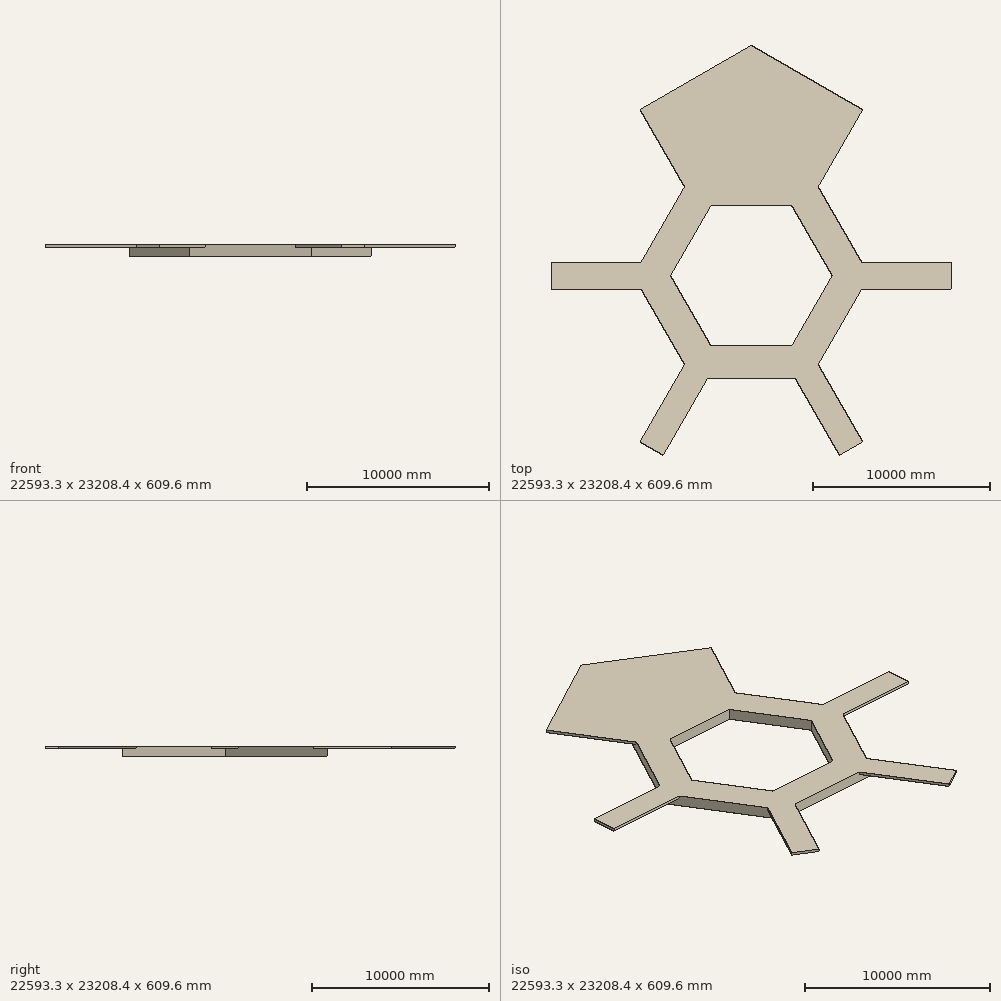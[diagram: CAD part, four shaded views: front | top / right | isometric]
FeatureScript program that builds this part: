
annotation { "Feature Type Name" : "Feature", "Feature Type Description" : "" }
export const myFeature = defineFeature(function(context is Context, id is Id, definition is map)
    precondition{}
    {
        {
            var Q0;
            Q0=qCreatedBy(makeId("Top.planeOp"),FACE);
            var sketch = newSketch(context, id + "F0", { "sketchPlane" : qUnion([Q0])});
            skCircle(sketch, "E0.cCircle", {"center": v(0, 0) * mm, "radius": 4575.39 * mm, "construction": true});
            skLineSegment(sketch, "E0.0", {"start": v(4575.39, 0) * mm, "end": v(2287.7, -3962.4) * mm});
            skLineSegment(sketch, "E0.1", {"start": v(2287.7, -3962.4) * mm, "end": v(-2287.7, -3962.4) * mm});
            skLineSegment(sketch, "E0.2", {"start": v(-2287.7, -3962.4) * mm, "end": v(-4575.39, 0) * mm});
            skLineSegment(sketch, "E0.3", {"start": v(-4575.39, 0) * mm, "end": v(-2287.7, 3962.4) * mm});
            skLineSegment(sketch, "E0.4", {"start": v(-2287.7, 3962.4) * mm, "end": v(2287.7, 3962.4) * mm});
            skLineSegment(sketch, "E0.5", {"start": v(2287.7, 3962.4) * mm, "end": v(4575.39, 0) * mm});
            skCircle(sketch, "E1.cCircle", {"center": v(0, 0) * mm, "radius": 6687.1 * mm, "construction": true});
            skLineSegment(sketch, "E1.0", {"start": v(6687.1, 0) * mm, "end": v(3343.55, -5791.2) * mm});
            skLineSegment(sketch, "E1.1", {"start": v(3343.55, -5791.2) * mm, "end": v(-3343.55, -5791.2) * mm});
            skLineSegment(sketch, "E1.2", {"start": v(-3343.55, -5791.2) * mm, "end": v(-6687.1, 0) * mm});
            skLineSegment(sketch, "E1.3", {"start": v(-6687.1, 0) * mm, "end": v(-3343.55, 5791.2) * mm});
            skLineSegment(sketch, "E1.4", {"start": v(-3343.55, 5791.2) * mm, "end": v(3343.55, 5791.2) * mm});
            skLineSegment(sketch, "E1.5", {"start": v(3343.55, 5791.2) * mm, "end": v(6687.1, 0) * mm});
            skLineSegment(sketch, "E2", {"start": v(-3783.5, 5029.2) * mm, "end": v(-6308.23, 9402.18) * mm});
            skLineSegment(sketch, "E3", {"start": v(-6308.23, 9402.18) * mm, "end": v(-4988.41, 10164.18) * mm});
            skLineSegment(sketch, "E4", {"start": v(-4988.41, 10164.18) * mm, "end": v(-2463.67, 5791.2) * mm});
            skLineSegment(sketch, "E5", {"start": v(-3343.55, 5791.2) * mm, "end": v(-5648.32, 9783.18) * mm, "construction": true});
            skLineSegment(sketch, "E6.1.0", {"start": v(-6687.1, 0) * mm, "end": v(-11296.64, 0) * mm, "construction": true});
            skLineSegment(sketch, "E6.1.1", {"start": v(-11296.64, -762) * mm, "end": v(-11296.64, 762) * mm});
            skLineSegment(sketch, "E6.1.2", {"start": v(-11296.64, 762) * mm, "end": v(-6247.16, 762) * mm});
            skLineSegment(sketch, "E6.1.3", {"start": v(-6247.16, -762) * mm, "end": v(-11296.64, -762) * mm});
            skLineSegment(sketch, "E6.2.0", {"start": v(-3343.55, -5791.2) * mm, "end": v(-5648.32, -9783.18) * mm, "construction": true});
            skLineSegment(sketch, "E6.2.1", {"start": v(-4988.41, -10164.18) * mm, "end": v(-6308.23, -9402.18) * mm});
            skLineSegment(sketch, "E6.2.2", {"start": v(-6308.23, -9402.18) * mm, "end": v(-3783.5, -5029.2) * mm});
            skLineSegment(sketch, "E6.2.3", {"start": v(-2463.67, -5791.2) * mm, "end": v(-4988.41, -10164.18) * mm});
            skLineSegment(sketch, "E6.3.0", {"start": v(3343.55, -5791.2) * mm, "end": v(5648.32, -9783.18) * mm, "construction": true});
            skLineSegment(sketch, "E6.3.1", {"start": v(6308.23, -9402.18) * mm, "end": v(4988.41, -10164.18) * mm});
            skLineSegment(sketch, "E6.3.2", {"start": v(4988.41, -10164.18) * mm, "end": v(2463.67, -5791.2) * mm});
            skLineSegment(sketch, "E6.3.3", {"start": v(3783.5, -5029.2) * mm, "end": v(6308.23, -9402.18) * mm});
            skLineSegment(sketch, "E6.4.0", {"start": v(6687.1, 0) * mm, "end": v(11296.64, 0) * mm, "construction": true});
            skLineSegment(sketch, "E6.4.1", {"start": v(11296.64, 762) * mm, "end": v(11296.64, -762) * mm});
            skLineSegment(sketch, "E6.4.2", {"start": v(11296.64, -762) * mm, "end": v(6247.16, -762) * mm});
            skLineSegment(sketch, "E6.4.3", {"start": v(6247.16, 762) * mm, "end": v(11296.64, 762) * mm});
            skLineSegment(sketch, "E6.5.0", {"start": v(3343.55, 5791.2) * mm, "end": v(5648.32, 9783.18) * mm, "construction": true});
            skLineSegment(sketch, "E6.5.1", {"start": v(4988.41, 10164.18) * mm, "end": v(6308.23, 9402.18) * mm});
            skLineSegment(sketch, "E6.5.2", {"start": v(6308.23, 9402.18) * mm, "end": v(3783.5, 5029.2) * mm});
            skLineSegment(sketch, "E6.5.3", {"start": v(2463.67, 5791.2) * mm, "end": v(4988.41, 10164.18) * mm});
            skLineSegment(sketch, "E7", {"start": v(-4988.41, 10164.18) * mm, "end": v(0, 13044.24) * mm});
            skLineSegment(sketch, "E8", {"start": v(0, 13044.24) * mm, "end": v(4988.41, 10164.18) * mm});
            skSolve(sketch);
        }
        {
            var Q0;
            Q0 = qSketchRegion(id + "F0", true);
            extrude(context, id + "F1", {"entities" : qUnion([Q0]), "depth" : 152.4 * mm});
        }
        {
            var Q0;
            Q0=makeQuery(id+"F0.imprint","IMPRINT",FACE,{"disambiguationData":[TD([[makeQuery(id+"F0.imprint","IMPRINT",EDGE,{"derivedFrom":sQuery(id+"F0.wireOp",EDGE,"E0.0")}),1.0]])]});
            extrude(context, id + "F2", {"entities" : qUnion([Q0]), "operationType" : NewBodyOperationType.ADD, "oppositeDirection" : true, "depth" : 457.2 * mm});
        }
        {
            var Q0;
            Q0=sQuery(id+"F0.wireOp",EDGE,"E4");
            var Q1;
            Q1=sQuery(id+"F0.wireOp",EDGE,"E6.5.3");
            var Q2;
            Q2=sQuery(id+"F0.wireOp",EDGE,"E6.5.2");
            var Q3;
            Q3=sQuery(id+"F0.wireOp",EDGE,"E6.4.3");
            var Q4;
            Q4=sQuery(id+"F0.wireOp",EDGE,"E6.4.2");
            extrude(context, id + "F3", {"bodyType" : ToolBodyType.SURFACE, "surfaceEntities" : qUnion([Q0, Q1, Q2, Q3, Q4]), "depth" : 3048 * mm});
        }
    });
